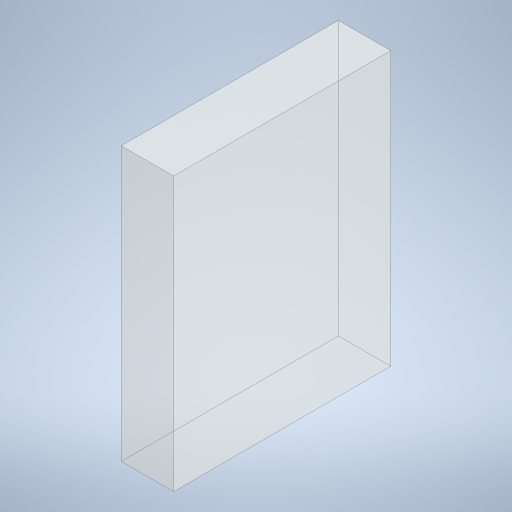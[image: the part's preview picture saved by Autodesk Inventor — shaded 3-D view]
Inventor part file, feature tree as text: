
AUTODESK INVENTOR PART (.ipt)
format: ipt  version: 2024 (Build 280153020, 153B)  size: 215,552 bytes
history: native  units: in
note: dims shown in document units (in); Inventor stores cm internally (conversion verified against a paired STEP export)
features: extrude x1, sketch x1
ambient origin geometry x8: Origin, YZ Plane, XZ Plane, XY Plane, X Axis, Y Axis, Z Axis, Center Point
bodies: Solid1 (feature_tree)
feature tree (2):
  extrude  "Extrusion1"  Depth=14.5in
  sketch  "Sketch1"  dims[d1=18.25in d2=14.5in d3=3.5in d4=0.0in]
